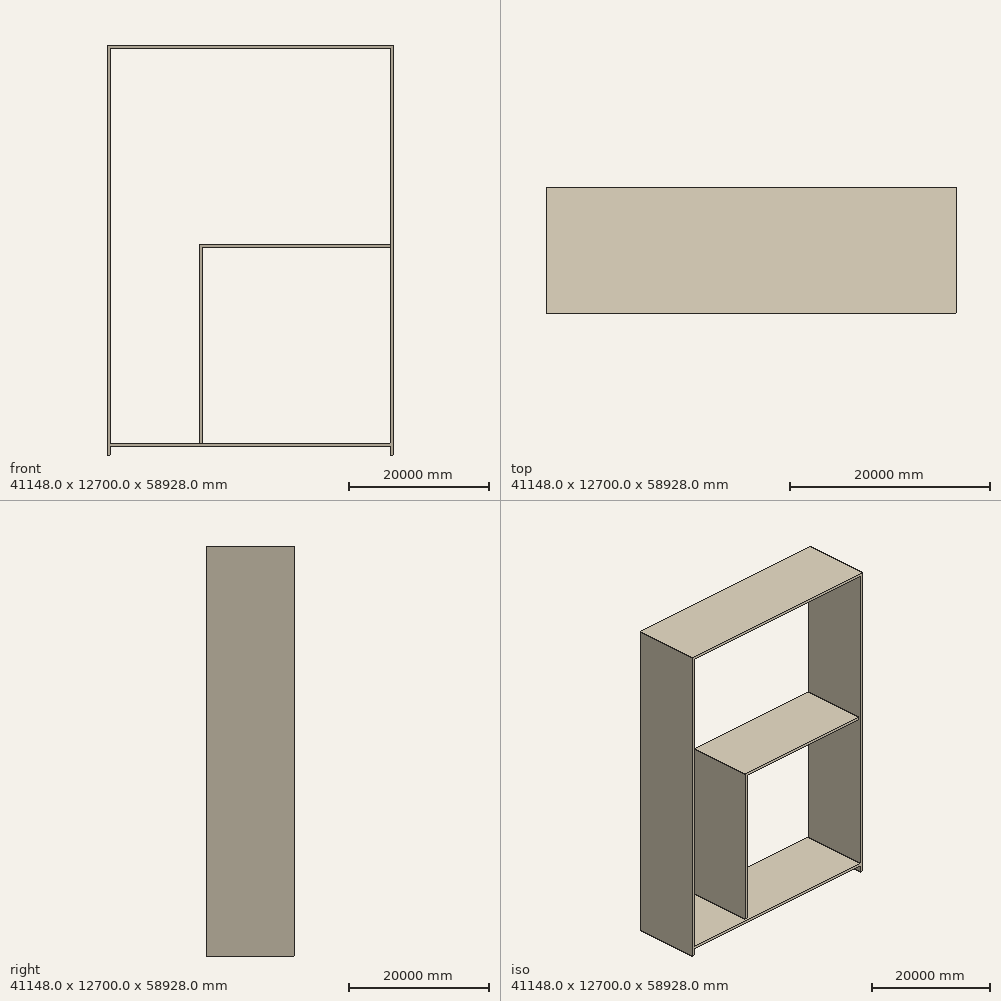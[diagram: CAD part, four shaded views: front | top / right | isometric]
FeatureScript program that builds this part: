
annotation { "Feature Type Name" : "Feature", "Feature Type Description" : "" }
export const myFeature = defineFeature(function(context is Context, id is Id, definition is map)
    precondition{}
    {
        {
            var Q0;
            Q0=qCreatedBy(makeId("Front.planeOp"),FACE);
            var sketch = newSketch(context, id + "F0", { "sketchPlane" : qUnion([Q0])});
            skLineSegment(sketch, "E0.bottom", {"start": v(-20574, 58928) * mm, "end": v(20574, 58928) * mm});
            skLineSegment(sketch, "E0.top", {"start": v(-20574, 0) * mm, "end": v(20574, 0) * mm});
            skLineSegment(sketch, "E0.left", {"start": v(-20574, 58928) * mm, "end": v(-20574, 0) * mm});
            skLineSegment(sketch, "E0.right", {"start": v(20574, 58928) * mm, "end": v(20574, 0) * mm});
            skSolve(sketch);
        }
        {
            var Q0;
            Q0=qCreatedBy(makeId("Front.planeOp"),FACE);
            var sketch = newSketch(context, id + "F1", { "sketchPlane" : qUnion([Q0])});
            skLineSegment(sketch, "E1.bottom", {"start": v(-20574, 0) * mm, "end": v(-20091.4, 0) * mm});
            skLineSegment(sketch, "E1.top", {"start": v(-20574, 58928) * mm, "end": v(-20091.4, 58928) * mm});
            skLineSegment(sketch, "E1.left", {"start": v(-20574, 0) * mm, "end": v(-20574, 58928) * mm});
            skLineSegment(sketch, "E1.right", {"start": v(-20091.4, 0) * mm, "end": v(-20091.4, 58928) * mm});
            skLineSegment(sketch, "E2.bottom", {"start": v(20574, 0) * mm, "end": v(20091.4, 0) * mm});
            skLineSegment(sketch, "E2.top", {"start": v(20574, 58928) * mm, "end": v(20091.4, 58928) * mm});
            skLineSegment(sketch, "E2.left", {"start": v(20574, 0) * mm, "end": v(20574, 58928) * mm});
            skLineSegment(sketch, "E2.right", {"start": v(20091.4, 0) * mm, "end": v(20091.4, 58928) * mm});
            skLineSegment(sketch, "E3.bottom", {"start": v(-20091.4, 1752.6) * mm, "end": v(20091.4, 1752.6) * mm});
            skLineSegment(sketch, "E3.top", {"start": v(-20091.4, 1270) * mm, "end": v(20091.4, 1270) * mm});
            skLineSegment(sketch, "E3.left", {"start": v(-20091.4, 1752.6) * mm, "end": v(-20091.4, 1270) * mm});
            skLineSegment(sketch, "E3.right", {"start": v(20091.4, 1752.6) * mm, "end": v(20091.4, 1270) * mm});
            skLineSegment(sketch, "E4.bottom", {"start": v(-20091.4, 58928) * mm, "end": v(20091.4, 58928) * mm});
            skLineSegment(sketch, "E4.top", {"start": v(-20091.4, 58445.4) * mm, "end": v(20091.4, 58445.4) * mm});
            skLineSegment(sketch, "E4.left", {"start": v(-20091.4, 58928) * mm, "end": v(-20091.4, 58445.4) * mm});
            skLineSegment(sketch, "E4.right", {"start": v(20091.4, 58928) * mm, "end": v(20091.4, 58445.4) * mm});
            skLineSegment(sketch, "E5.bottom", {"start": v(-20091.4, 56540.4) * mm, "end": v(20091.4, 56540.4) * mm});
            skLineSegment(sketch, "E5.top", {"start": v(-20091.4, 55778.4) * mm, "end": v(20091.4, 55778.4) * mm});
            skLineSegment(sketch, "E5.left", {"start": v(-20091.4, 56540.4) * mm, "end": v(-20091.4, 55778.4) * mm});
            skLineSegment(sketch, "E5.right", {"start": v(20091.4, 56540.4) * mm, "end": v(20091.4, 55778.4) * mm});
            skLineSegment(sketch, "E6.bottom", {"start": v(-6908.8, 1752.6) * mm, "end": v(-7391.4, 1752.6) * mm});
            skLineSegment(sketch, "E6.top", {"start": v(-6908.8, 29895.8) * mm, "end": v(-7391.4, 29895.8) * mm});
            skLineSegment(sketch, "E6.left", {"start": v(-6908.8, 1752.6) * mm, "end": v(-6908.8, 29895.8) * mm});
            skLineSegment(sketch, "E6.right", {"start": v(-7391.4, 1752.6) * mm, "end": v(-7391.4, 29895.8) * mm});
            skLineSegment(sketch, "E7.bottom", {"start": v(-7391.4, 29895.8) * mm, "end": v(20091.4, 29895.8) * mm});
            skLineSegment(sketch, "E7.top", {"start": v(-7391.4, 30378.4) * mm, "end": v(20091.4, 30378.4) * mm});
            skLineSegment(sketch, "E7.left", {"start": v(-7391.4, 29895.8) * mm, "end": v(-7391.4, 30378.4) * mm});
            skLineSegment(sketch, "E7.right", {"start": v(20091.4, 29895.8) * mm, "end": v(20091.4, 30378.4) * mm});
            skLineSegment(sketch, "E8.bottom", {"start": v(-6908.8, 27990.8) * mm, "end": v(20091.4, 27990.8) * mm});
            skLineSegment(sketch, "E8.top", {"start": v(-6908.8, 27228.8) * mm, "end": v(20091.4, 27228.8) * mm});
            skLineSegment(sketch, "E8.left", {"start": v(-6908.8, 27990.8) * mm, "end": v(-6908.8, 27228.8) * mm});
            skLineSegment(sketch, "E8.right", {"start": v(20091.4, 27990.8) * mm, "end": v(20091.4, 27228.8) * mm});
            skSolve(sketch);
        }
        {
            var Q0;
            {var subQ7=sQuery(id+"F1.wireOp",EDGE,"E2.bottom");var subQ8=sQuery(id+"F1.wireOp",EDGE,"E3.top");var subQ18=sQuery(id+"F1.wireOp",EDGE,"E4.bottom");var subQ28=sQuery(id+"F1.wireOp",EDGE,"E1.bottom");Q0=qUnion([makeQuery(id+"F1.imprint","IMPRINT",FACE,{"disambiguationData":[TD([[makeQuery(id+"F1.imprint","IMPRINT",EDGE,{"derivedFrom":subQ18}),-1.0]])]}),makeQuery(id+"F1.imprint","IMPRINT",FACE,{"disambiguationData":[TD([[makeQuery(id+"F1.imprint","IMPRINT",EDGE,{"derivedFrom":subQ28}),1.0]])]}),makeQuery(id+"F1.imprint","IMPRINT",FACE,{"disambiguationData":[TD([[makeQuery(id+"F1.imprint","IMPRINT",EDGE,{"derivedFrom":subQ8}),1.0]])]}),makeQuery(id+"F1.imprint","IMPRINT",FACE,{"disambiguationData":[TD([[makeQuery(id+"F1.imprint","IMPRINT",EDGE,{"derivedFrom":subQ7}),-1.0]])]})]);}
            extrude(context, id + "F2", {"entities" : qUnion([Q0]), "depth" : 12700 * mm, "offsetDistance" : 25.4 * mm});
        }
        {
            var Q0;
            {var subQ1=sQuery(id+"F1.wireOp",EDGE,"E6.top");Q0=makeQuery(id+"F1.imprint","IMPRINT",FACE,{"disambiguationData":[TD([[makeQuery(id+"F1.imprint","IMPRINT",EDGE,{"derivedFrom":subQ1}),1.0]])]});}
            var Q1;
            Q1=makeQuery(id+"F1.imprint","IMPRINT",FACE,{"disambiguationData":[TD([[makeQuery(id+"F1.imprint","IMPRINT",EDGE,{"derivedFrom":sQuery(id+"F1.wireOp",EDGE,"E6.top")}),-1.0]])]});
            extrude(context, id + "F3", {"entities" : qUnion([Q0, Q1]), "operationType" : NewBodyOperationType.ADD, "depth" : 12192 * mm, "offsetDistance" : 25.4 * mm});
        }
    });
